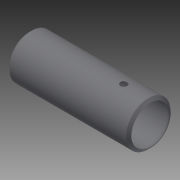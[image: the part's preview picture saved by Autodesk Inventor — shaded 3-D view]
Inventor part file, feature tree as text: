
AUTODESK INVENTOR PART (.ipt)
format: ipt  version: 2014 (Build 180170000, 170)  size: 137,216 bytes
history: native  units: in
note: dims shown in document units (in); Inventor stores cm internally (conversion verified against a paired STEP export)
features: other x56, revolve x2, sketch x2
ambient origin geometry x8: Origin, YZ Plane, XZ Plane, XY Plane, X Axis, Y Axis, Z Axis, Center Point
bodies: Solid1 (feature_tree)
feature tree (60):
  revolve  "Revolution1"  Angle=360.0deg
  revolve  "Revolution2"  [1 undecoded]
  other  "o1_XY"
  other  "o1_YZ"
  other  "o1_ZX"
  other  "o1_X"
  other  "o1_Y"
  other  "o1_Z"
  other  "o1_Center"
  other  "o2_XY"
  other  "o2_YZ"
  other  "o2_ZX"
  other  "o2_X"
  other  "o2_Y"
  other  "o2_Z"
  other  "o2_Center"
  other  "t1_XY"
  other  "t1_YZ"
  other  "t1_ZX"
  other  "t1_X"
  other  "t1_Y"
  other  "t1_Z"
  other  "t1_Center"
  other  "t2_XY"
  other  "t2_YZ"
  other  "t2_ZX"
  other  "t2_X"
  other  "t2_Y"
  other  "t2_Z"
  other  "t2_Center"
  other  "t3_XY"
  other  "t3_YZ"
  other  "t3_ZX"
  other  "t3_X"
  other  "t3_Y"
  other  "t3_Z"
  other  "t3_Center"
  other  "t4_XY"
  other  "t4_YZ"
  other  "t4_ZX"
  other  "t4_X"
  other  "t4_Y"
  other  "t4_Z"
  other  "t4_Center"
  other  "tube1_XY"
  other  "tube1_YZ"
  other  "tube1_ZX"
  other  "tube1_X"
  other  "tube1_Y"
  other  "tube1_Z"
  other  "tube1_Center"
  other  "tube2_XY"
  other  "tube2_YZ"
  other  "tube2_ZX"
  other  "tube2_X"
  other  "tube2_Y"
  other  "tube2_Z"
  other  "tube2_Center"
  sketch  "Sketch_5"
  sketch  "Sketch_1"  dims[d0=360.0deg d1=360.0deg]
note: 1 required parameter value undecoded (feature->parameter linkage not recoverable at this tier; creation-order binding heuristic only, values carry confidence <= 0.55)
